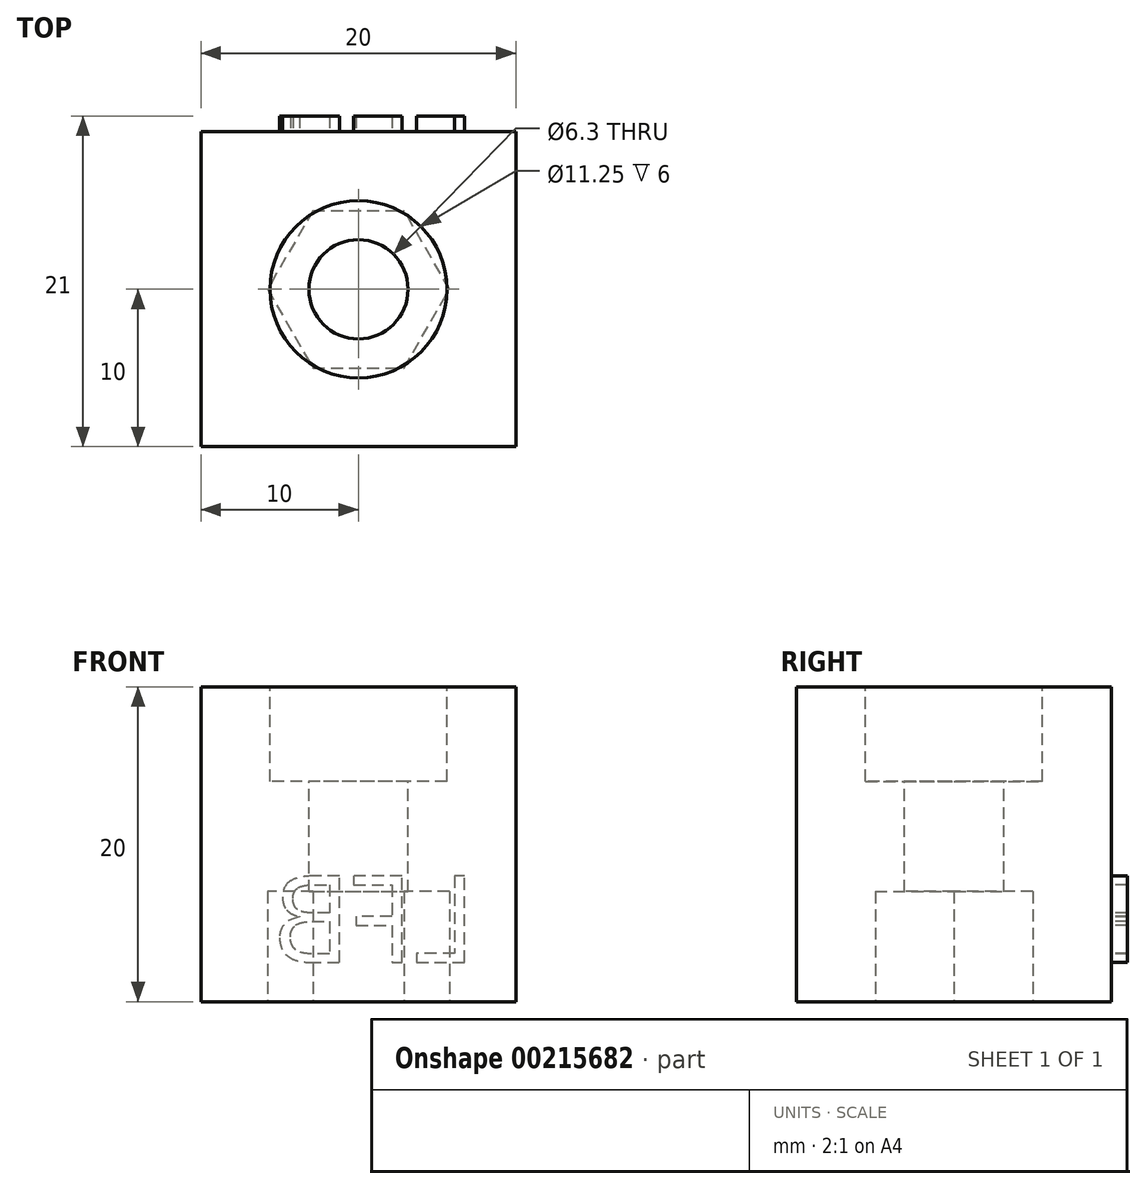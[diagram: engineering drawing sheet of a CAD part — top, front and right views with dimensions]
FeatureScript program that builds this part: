
annotation { "Feature Type Name" : "Feature", "Feature Type Description" : "" }
export const myFeature = defineFeature(function(context is Context, id is Id, definition is map)
    precondition{}
    {
        {
            var Q0;
            Q0=qCreatedBy(makeId("Top.planeOp"),FACE);
            var sketch = newSketch(context, id + "F0", { "sketchPlane" : qUnion([Q0])});
            skLineSegment(sketch, "E0.bottom", {"start": v(0, 0) * mm, "end": v(20, 0) * mm});
            skLineSegment(sketch, "E0.top", {"start": v(0, 20) * mm, "end": v(20, 20) * mm});
            skLineSegment(sketch, "E0.left", {"start": v(0, 0) * mm, "end": v(0, 20) * mm});
            skLineSegment(sketch, "E0.right", {"start": v(20, 0) * mm, "end": v(20, 20) * mm});
            skSolve(sketch);
        }
        {
            var Q0;
            Q0=makeQuery(id+"F0.imprint","IMPRINT",FACE,{"disambiguationData":[TD([[makeQuery(id+"F0.imprint","IMPRINT",EDGE,{"derivedFrom":sQuery(id+"F0.wireOp",EDGE,"E0.bottom")}),1.0]])]});
            extrude(context, id + "F1", {"entities" : qUnion([Q0]), "depth" : 20 * mm});
        }
        {
            var Q0;
            Q0=makeQuery(id+"F1.opExtrude","CAP_FACE",FACE,{"disambiguationData":[OSD([sQuery(id+"F0.wireOp",EDGE,"E0.bottom"),sQuery(id+"F0.wireOp",EDGE,"E0.top"),sQuery(id+"F0.wireOp",EDGE,"E0.left"),sQuery(id+"F0.wireOp",EDGE,"E0.right")])],"isStart":false});
            var sketch = newSketch(context, id + "F2", { "sketchPlane" : qUnion([Q0])});
            skPoint(sketch, "E1", {"position": v(10, 10) * mm});
            skPoint(sketch, "E1.positionSnap0", {"position": v(20, 10) * mm});
            skSolve(sketch);
        }
        {
            var Q0;
            Q0=sQuery(id+"F2.wireOp",VERTEX,"E1");
            var Q1;
            Q1=makeQuery(id+"F1.opExtrude","SWEPT_BODY",BODY,{"disambiguationData":[OSD([sQuery(id+"F0.wireOp",EDGE,"E0.bottom"),sQuery(id+"F0.wireOp",EDGE,"E0.top"),sQuery(id+"F0.wireOp",EDGE,"E0.left"),sQuery(id+"F0.wireOp",EDGE,"E0.right")])]});
            hole(context, id + "F3", {"style" : HoleStyle.C_BORE, "endStyle" : HoleEndStyle.THROUGH, "standardTappedOrClearance" : lookupTablePath({ "standard" : "ISO", "fit" : "Close", "size" : "M6", "type" : "Clearance" }), "standardBlindInLast" : lookupTablePath({ "fit" : "Close", "standard" : "ISO", "size" : "M6", "type" : "Clearance" }), "holeDiameter" : 6.3 * mm, "cBoreDiameter" : 11.25 * mm, "cBoreDepth" : 6 * mm, "locations" : qUnion([Q0]), "scope" : qUnion([Q1]), "isTappedThrough" : true});
        }
        {
            var Q0;
            Q0=makeQuery(id+"F1.opExtrude","CAP_FACE",FACE,{"disambiguationData":[OSD([sQuery(id+"F0.wireOp",EDGE,"E0.bottom"),sQuery(id+"F0.wireOp",EDGE,"E0.top"),sQuery(id+"F0.wireOp",EDGE,"E0.left"),sQuery(id+"F0.wireOp",EDGE,"E0.right")])],"isStart":true});
            var sketch = newSketch(context, id + "F4", { "sketchPlane" : qUnion([Q0])});
            skPoint(sketch, "E2.0.midPoint", {"position": v(10, -10) * mm});
            skCircle(sketch, "E3", {"center": v(10, -10) * mm, "radius": 5 * mm});
            skLineSegment(sketch, "E4", {"start": v(10, -10) * mm, "end": v(10, -5) * mm, "construction": true});
            skLineSegment(sketch, "E5", {"start": v(10, -10) * mm, "end": v(10, -15) * mm, "construction": true});
            skLineSegment(sketch, "E6", {"start": v(4.22, -10) * mm, "end": v(7.11, -5) * mm});
            skLineSegment(sketch, "E7", {"start": v(12.89, -5) * mm, "end": v(15.78, -10) * mm});
            skLineSegment(sketch, "E8", {"start": v(15.78, -10) * mm, "end": v(12.89, -15) * mm});
            skLineSegment(sketch, "E9", {"start": v(7.11, -15) * mm, "end": v(4.22, -10) * mm});
            skLineSegment(sketch, "E10", {"start": v(7.11, -5) * mm, "end": v(12.89, -5) * mm});
            skLineSegment(sketch, "E11", {"start": v(7.11, -15) * mm, "end": v(12.89, -15) * mm});
            skSolve(sketch);
        }
        {
            var Q0;
            Q0 = qSketchRegion(id + "F4", true);
            extrude(context, id + "F5", {"entities" : qUnion([Q0]), "operationType" : NewBodyOperationType.REMOVE, "oppositeDirection" : true, "depth" : 7 * mm});
        }
        {
            var Q0;
            Q0=makeQuery(id+"F1.opExtrude","SWEPT_FACE",FACE,{"disambiguationData":[OSD([sQuery(id+"F0.wireOp",EDGE,"E0.top")])]});
            var sketch = newSketch(context, id + "F6", { "sketchPlane" : qUnion([Q0])});
            skText(sketch, "E12", { "text": "LFB", "fontName": "OpenSans-Regular.ttf"});
            const initialGuessF6  = {"E12": [-0.0175, 0.0025, 1, 0, 0.00553]};
            skSetInitialGuess(sketch, initialGuessF6);
            skSolve(sketch);
        }
        {
            var Q0;
            Q0 = qSketchRegion(id + "F6", true);
            extrude(context, id + "F7", {"entities" : qUnion([Q0]), "operationType" : NewBodyOperationType.ADD, "depth" : 1 * mm});
        }
    });
